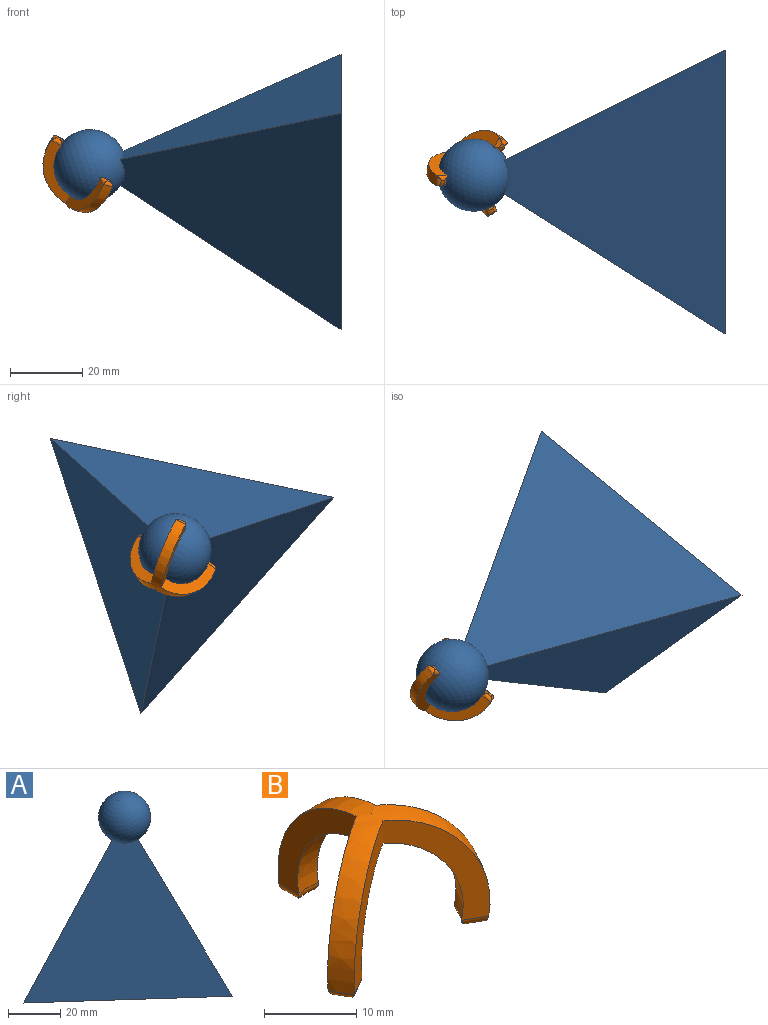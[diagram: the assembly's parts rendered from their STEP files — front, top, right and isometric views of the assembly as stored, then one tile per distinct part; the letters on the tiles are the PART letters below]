
ASSEMBLY  parts=2 mates=1
PART A: 19 faces, bbox 76x78.3x79.3 mm
  f0: plane 78.32x75.98mm, normal (0,0,-1), area 2307.5mm2, adj f1,f2,f3,f4
  f1: plane 60.96x59.68mm, normal (-0.63,-0.71,0.32), area 2871.1mm2, adj f0,f2,f3,f18
  f2: plane 78.32x60.96mm, normal (0.93,-0.19,0.32), area 2871.1mm2, adj f0,f1,f3,f18
  f3: plane 75.98x60.96mm, normal (-0.3,0.9,0.32), area 2871.1mm2, adj f0,f1,f2,f18
  f4: cylinder r=12.15mm len=24.3mm, axis (0,0,1), area 1855.1mm2, adj f0,f6
  f5: cylinder r=2mm len=11.79mm, axis (0,0,-1), area 148.1mm2, adj f16,f17
  f6: plane 24.3x24.3mm, normal (0,0,-1), area 209.3mm2, adj f4,f12
  f7: cylinder r=1.1mm len=19.73mm, axis (0,0,1), area 136.4mm2, adj f15,f16
  f8: cylinder r=9mm len=18mm, axis (0,0,1), area 322.3mm2, adj f9,f10
  f9: plane 18x18mm, normal (0,0,1), area 100.5mm2, adj f8,f11
  f10: plane 18x18mm, normal (0,0,-1), area 226.2mm2, adj f8,f14
  f11: cylinder r=7mm len=14mm, axis (0,0,1), area 175.9mm2, adj f9,f13
  f12: cylinder r=9mm len=18mm, axis (0,0,1), area 395.8mm2, adj f6,f13
  f13: plane 18x18mm, normal (0,0,-1), area 100.5mm2, adj f11,f12
  f14: cylinder r=3mm len=6.69mm, axis (0,0,1), area 126mm2, adj f10,f15
  f15: cone r=3.39mm half-angle=45deg, axis (0,0,1), area 34.6mm2, adj f7,f14
  f16: cone r=2.39mm half-angle=45deg, axis (0,0,-1), area 12.4mm2, adj f5,f7
  f17: plane 4x4mm, normal (0,0,-1), area 12.6mm2, adj f5
  f18: sphere r=10mm, area 1206.8mm2, adj f1,f2,f3
PART B: 23 faces, bbox 26x26x16 mm
  f0: sphere r=10mm, area 154mm2, adj f1,f2,f3,f4,f5,f6,f11,f15
  f1: plane 14.89x10.43mm, normal (0.5,-0.87,0), area 57.7mm2, adj f0,f2,f10,f15,f17
  f2: plane 14.89x10.43mm, normal (-0.5,-0.87,0), area 57.7mm2, adj f0,f1,f10,f19,f20
  f3: plane 14.89x10.43mm, normal (0.5,0.87,0), area 57.7mm2, adj f0,f4,f10,f19,f21
  f4: plane 14.89x12.05mm, normal (1,0,0), area 57.7mm2, adj f0,f3,f10,f11,f12
  f5: plane 14.89x12.05mm, normal (-1,0,0), area 57.7mm2, adj f0,f6,f10,f11,f13
  f6: plane 14.89x10.43mm, normal (-0.5,0.87,0), area 57.7mm2, adj f0,f5,f10,f15,f16
  f7: plane 1.03x1mm, normal (0,0,-1), area 1mm2, adj f11,f12,f13,f14
  f8: plane 1.38x1.37mm, normal (0,0,-1), area 1mm2, adj f15,f16,f17,f18
  f9: plane 1.38x1.37mm, normal (0,0,-1), area 1mm2, adj f19,f20,f21,f22
  f10: sphere r=13mm, area 199.5mm2, adj f1,f2,f3,f4,f5,f6,f12,f13
  f11: torus R=10.82mm, axis (0,0,1), area 4.1mm2, adj f0,f4,f5,f7,f12,f13
  f12: cylinder r=1mm len=3.06mm, axis (0,1,0), area 3.6mm2, adj f4,f7,f10,f11,f14
  f13: cylinder r=1mm len=3.06mm, axis (0,-1,0), area 3.6mm2, adj f5,f7,f10,f11,f14
  f14: torus R=11.83mm, axis (0,0,1), area 3.1mm2, adj f7,f10,f12,f13
  f15: torus R=10.82mm, axis (0,0,1), area 4.1mm2, adj f0,f1,f6,f8,f16,f17
  f16: cylinder r=1mm len=3.15mm, axis (-0.87,-0.5,0), area 3.6mm2, adj f6,f8,f10,f15,f18
  f17: cylinder r=1mm len=3.15mm, axis (0.87,0.5,0), area 3.6mm2, adj f1,f8,f10,f15,f18
  f18: torus R=11.83mm, axis (0,0,1), area 3.1mm2, adj f8,f10,f16,f17
  f19: torus R=10.82mm, axis (0,0,1), area 4.1mm2, adj f0,f2,f3,f9,f20,f21
  f20: cylinder r=1mm len=3.15mm, axis (0.87,-0.5,0), area 3.6mm2, adj f2,f9,f10,f19,f22
  f21: cylinder r=1mm len=3.15mm, axis (-0.87,0.5,0), area 3.6mm2, adj f3,f9,f10,f19,f22
  f22: torus R=11.83mm, axis (0,0,1), area 3.1mm2, adj f9,f10,f20,f21
PLACE A rot(axis=(0,-1,0),90deg) t=(66.36,39.36,62.51)mm
PLACE B rot(axis=(-0.28,-0.95,-0.14),146.7deg) t=(-2.92,39.36,62.51)mm
MATE ball B.f11 <-> A.f4  axis (-0.45,0.41,-0.8) through (-2.92,39.36,62.51)mm
